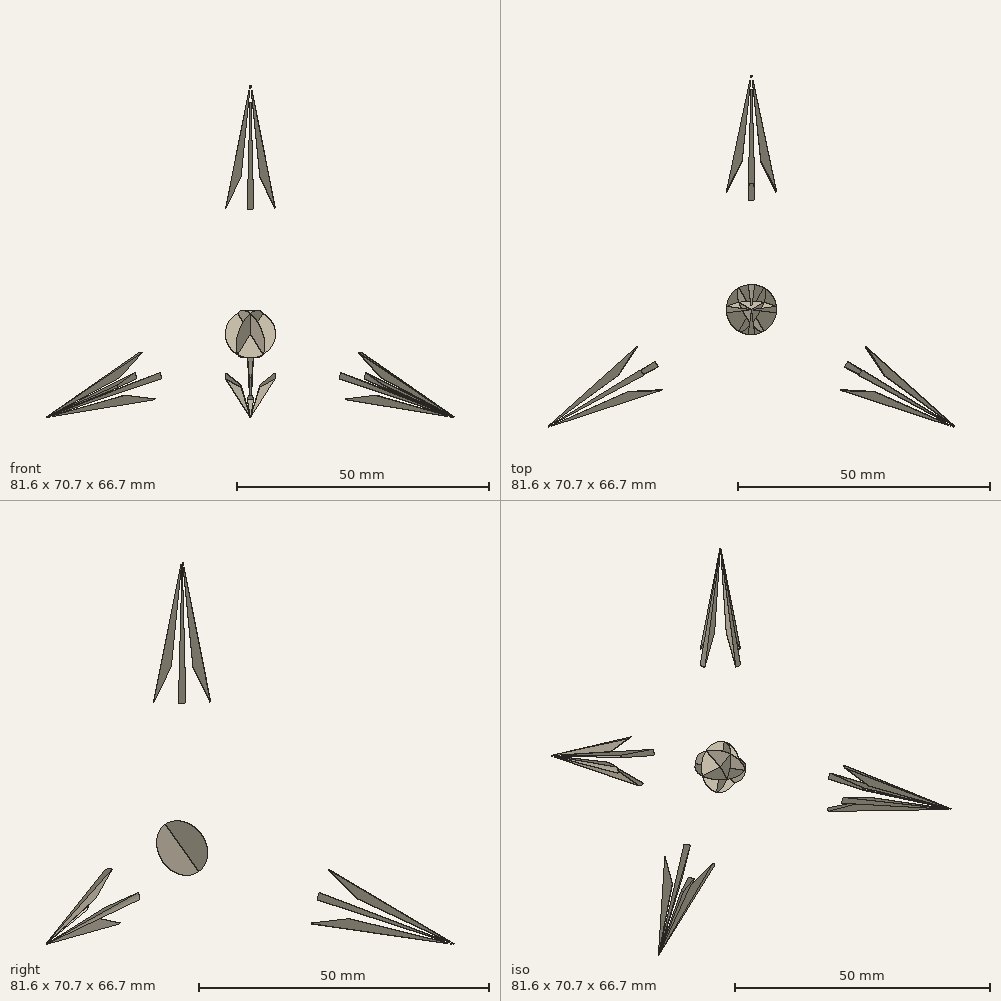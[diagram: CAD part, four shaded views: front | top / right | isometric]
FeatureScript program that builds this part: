
annotation { "Feature Type Name" : "Feature", "Feature Type Description" : "" }
export const myFeature = defineFeature(function(context is Context, id is Id, definition is map)
    precondition{}
    {
        {
            var Q0;
            Q0=qCreatedBy(makeId("Front.planeOp"),FACE);
            var sketch = newSketch(context, id + "F0", { "sketchPlane" : qUnion([Q0])});
            skCircle(sketch, "E0", {"center": v(0, 0) * mm, "radius": 50 * mm});
            skLineSegment(sketch, "E1", {"start": v(0, 0) * mm, "end": v(-5, 0) * mm});
            skLineSegment(sketch, "E2", {"start": v(0, 0) * mm, "end": v(5, 0) * mm});
            skLineSegment(sketch, "E3", {"start": v(-5, 0) * mm, "end": v(-5, 12.44) * mm});
            skLineSegment(sketch, "E4", {"start": v(5, 0) * mm, "end": v(5, 12.44) * mm});
            skLineSegment(sketch, "E5", {"start": v(-5, 24.87) * mm, "end": v(-5, 49.75) * mm, "construction": true});
            skLineSegment(sketch, "E6", {"start": v(-5, 12.44) * mm, "end": v(-5, 24.87) * mm});
            skLineSegment(sketch, "E7", {"start": v(5, 24.87) * mm, "end": v(5, 49.75) * mm, "construction": true});
            skLineSegment(sketch, "E8", {"start": v(5, 12.44) * mm, "end": v(5, 24.87) * mm});
            skLineSegment(sketch, "E9", {"start": v(0, 50) * mm, "end": v(-1.25, 37.5) * mm});
            skLineSegment(sketch, "E10", {"start": v(0, 50) * mm, "end": v(1.25, 37.5) * mm});
            skLineSegment(sketch, "E11", {"start": v(-5, 24.87) * mm, "end": v(0, 50) * mm});
            skLineSegment(sketch, "E12", {"start": v(0, 50) * mm, "end": v(5, 24.87) * mm});
            skLineSegment(sketch, "E13", {"start": v(-2.5, 25) * mm, "end": v(-5, 0) * mm});
            skLineSegment(sketch, "E14", {"start": v(2.5, 25) * mm, "end": v(5, 0) * mm});
            skLineSegment(sketch, "E15", {"start": v(1.25, 37.5) * mm, "end": v(1.88, 31.25) * mm});
            skLineSegment(sketch, "E16", {"start": v(-1.25, 37.5) * mm, "end": v(-1.87, 31.25) * mm});
            skLineSegment(sketch, "E17", {"start": v(-1.88, 31.25) * mm, "end": v(-2.5, 25) * mm});
            skLineSegment(sketch, "E18", {"start": v(1.88, 31.25) * mm, "end": v(2.5, 25) * mm});
            skLineSegment(sketch, "E19", {"start": v(-1.87, 31.25) * mm, "end": v(-5, 24.87) * mm});
            skLineSegment(sketch, "E20", {"start": v(1.88, 31.25) * mm, "end": v(5, 24.87) * mm});
            skLineSegment(sketch, "E21", {"start": v(0, 50) * mm, "end": v(0, 0) * mm});
            skLineSegment(sketch, "E22", {"start": v(50, 0) * mm, "end": v(-50, 0) * mm});
            skSolve(sketch);
        }
        {
            var Q0;
            Q0=makeQuery(id+"F0.imprint","IMPRINT",FACE,{"disambiguationData":[TD([[makeQuery(id+"F0.imprint","IMPRINT",EDGE,{"derivedFrom":sQuery(id+"F0.wireOp",EDGE,"E9")}),1.0]])]});
            var Q1;
            Q1=sQuery(id+"F0.wireOp",EDGE,"E21");
            revolve(context, id + "F1", {"surfaceOperationType" : NewSurfaceOperationType.NEW, "entities" : qUnion([Q0]), "axis" : qUnion([Q1]), "revolveType" : RevolveType.FULL});
        }
        {
            var Q0;
            Q0=makeQuery(id+"F0.imprint","IMPRINT",FACE,{"disambiguationData":[TD([[makeQuery(id+"F0.imprint","IMPRINT",EDGE,{"derivedFrom":sQuery(id+"F0.wireOp",EDGE,"E10")}),1.0]])]});
            var Q1;
            Q1=sQuery(id+"F0.wireOp",EDGE,"E21");
            revolve(context, id + "F2", {"surfaceOperationType" : NewSurfaceOperationType.NEW, "entities" : qUnion([Q0]), "axis" : qUnion([Q1]), "revolveType" : RevolveType.SYMMETRIC, "angle" : 15 * degree});
        }
        {
            var Q0;
            Q0=makeQuery(id+"F2.opRevolve","SWEPT_BODY",BODY,{"disambiguationData":[OSD([sQuery(id+"F0.wireOp",EDGE,"E10"),sQuery(id+"F0.wireOp",EDGE,"E12"),sQuery(id+"F0.wireOp",EDGE,"E15"),sQuery(id+"F0.wireOp",EDGE,"E20")])]});
            var Q1;
            Q1=sQuery(id+"F0.wireOp",EDGE,"E21");
            circularPattern(context, id + "F3", {"operationType" : NewBodyOperationType.ADD, "entities" : qUnion([Q0]), "axis" : qUnion([Q1]), "angle" : 360 * degree, "instanceCount" : 4, "equalSpace" : true});
        }
        {
            var Q0;
            Q0=makeQuery(id+"F1.opRevolve","SWEPT_BODY",BODY,{"disambiguationData":[OSD([sQuery(id+"F0.wireOp",EDGE,"E1"),sQuery(id+"F0.wireOp",EDGE,"E9"),sQuery(id+"F0.wireOp",EDGE,"E13"),sQuery(id+"F0.wireOp",EDGE,"E16"),sQuery(id+"F0.wireOp",EDGE,"E17"),sQuery(id+"F0.wireOp",EDGE,"E21")])]});
            var Q1;
            Q1=sQuery(id+"F0.wireOp",EDGE,"E22");
            transform(context, id + "F4", {"entities" : qUnion([Q0]), "transformType" : TransformType.ROTATION, "transformAxis" : qUnion([Q1]), "angle" : 109.47 * degree, "makeCopy" : true});
        }
        {
            var Q0;
            Q0=makeQuery(id+"F4.opPattern","COPY",BODY,{"derivedFrom":makeQuery(id+"F1.opRevolve","SWEPT_BODY",BODY,{"disambiguationData":[OSD([sQuery(id+"F0.wireOp",EDGE,"E9"),sQuery(id+"F0.wireOp",EDGE,"E13"),sQuery(id+"F0.wireOp",EDGE,"E16"),sQuery(id+"F0.wireOp",EDGE,"E17"),sQuery(id+"F0.wireOp",EDGE,"E21"),sQuery(id+"F0.wireOp",EDGE,"E22")])]}),"instanceName":"1"});
            var Q1;
            Q1=sQuery(id+"F0.wireOp",EDGE,"E21");
            circularPattern(context, id + "F5", {"entities" : qUnion([Q0]), "axis" : qUnion([Q1]), "angle" : 360 * degree, "instanceCount" : 3, "equalSpace" : true});
        }
    });
